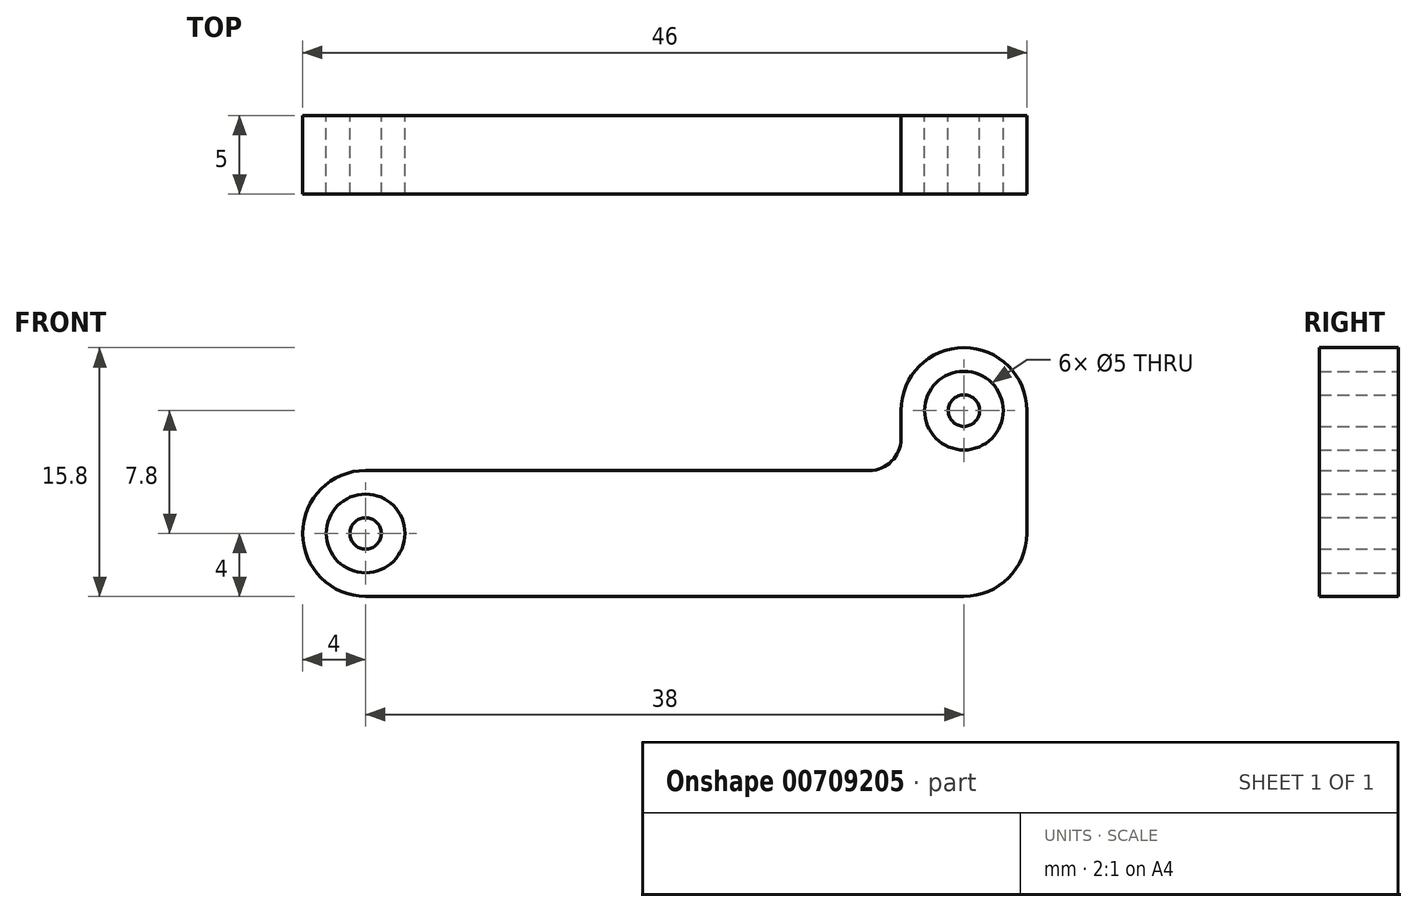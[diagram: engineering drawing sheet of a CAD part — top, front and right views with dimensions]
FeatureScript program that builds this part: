
annotation { "Feature Type Name" : "Feature", "Feature Type Description" : "" }
export const myFeature = defineFeature(function(context is Context, id is Id, definition is map)
    precondition{}
    {
        {
            var Q0;
            Q0=qCreatedBy(makeId("Front.planeOp"),FACE);
            var sketch = newSketch(context, id + "F0", { "sketchPlane" : qUnion([Q0])});
            skArc(sketch, "E0", {"start": v(0, 4) * mm, "mid": v(-4, 0) * mm, "end": v(0, -4) * mm});
            skArc(sketch, "E1", {"start": v(42, 7.8) * mm, "mid": v(38, 11.8) * mm, "end": v(34, 7.8) * mm});
            skLineSegment(sketch, "E2", {"start": v(0, 4) * mm, "end": v(32, 4) * mm});
            skLineSegment(sketch, "E3", {"start": v(34, 7.8) * mm, "end": v(34, 6) * mm});
            skLineSegment(sketch, "E4", {"start": v(0, -4) * mm, "end": v(38, -4) * mm});
            skLineSegment(sketch, "E5", {"start": v(42, 7.8) * mm, "end": v(42, 0) * mm});
            skPoint(sketch, "E6.visualSharp", {"position": v(34, 4) * mm});
            skArc(sketch, "E6.filletArc", {"start": v(32, 4) * mm, "mid": v(33.41, 4.59) * mm, "end": v(34, 6) * mm});
            skPoint(sketch, "E7.visualSharp", {"position": v(42, -4) * mm});
            skArc(sketch, "E7.filletArc", {"start": v(38, -4) * mm, "mid": v(40.83, -2.83) * mm, "end": v(42, 0) * mm});
            skCircle(sketch, "E8", {"center": v(0, 0) * mm, "radius": 2.5 * mm});
            skCircle(sketch, "E9", {"center": v(0, 0) * mm, "radius": 1 * mm});
            skCircle(sketch, "E10", {"center": v(38, 7.8) * mm, "radius": 2.5 * mm});
            skCircle(sketch, "E11", {"center": v(38, 7.8) * mm, "radius": 1 * mm});
            skSolve(sketch);
        }
        {
            var Q0;
            Q0=makeQuery(id+"F0.imprint","IMPRINT",FACE,{"disambiguationData":[TD([[makeQuery(id+"F0.imprint","IMPRINT",EDGE,{"derivedFrom":sQuery(id+"F0.wireOp",EDGE,"E0")}),1.0]])]});
            var Q1;
            Q1=makeQuery(id+"F0.imprint","IMPRINT",FACE,{"disambiguationData":[TD([[makeQuery(id+"F0.imprint","IMPRINT",EDGE,{"derivedFrom":sQuery(id+"F0.wireOp",EDGE,"E9")}),1.0]])]});
            var Q2;
            Q2=makeQuery(id+"F0.imprint","IMPRINT",FACE,{"disambiguationData":[TD([[makeQuery(id+"F0.imprint","IMPRINT",EDGE,{"derivedFrom":sQuery(id+"F0.wireOp",EDGE,"E11")}),1.0]])]});
            extrude(context, id + "F1", {"entities" : qUnion([Q0, Q1, Q2]), "depth" : 5 * mm, "offsetDistance" : 25 * mm});
        }
    });
